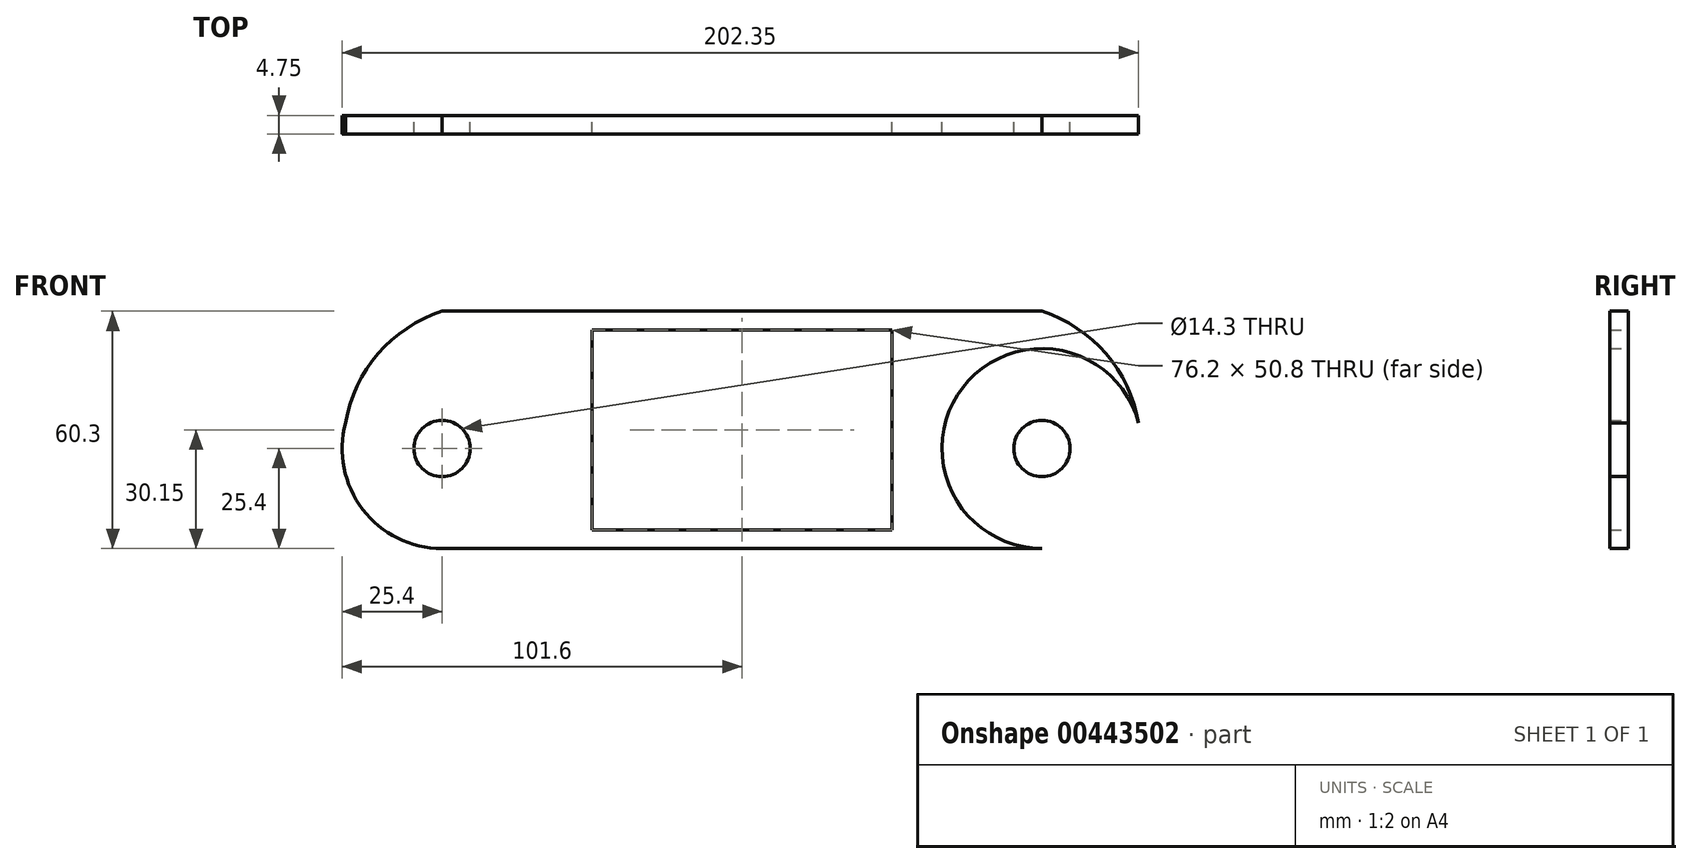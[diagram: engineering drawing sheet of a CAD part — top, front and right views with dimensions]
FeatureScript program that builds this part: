
annotation { "Feature Type Name" : "Feature", "Feature Type Description" : "" }
export const myFeature = defineFeature(function(context is Context, id is Id, definition is map)
    precondition{}
    {
        {
            var Q0;
            Q0=qCreatedBy(makeId("Front.planeOp"),FACE);
            var sketch = newSketch(context, id + "F0", { "sketchPlane" : qUnion([Q0])});
            skLineSegment(sketch, "E0.bottom", {"start": v(-38.1, 30.15) * mm, "end": v(38.1, 30.15) * mm});
            skLineSegment(sketch, "E0.top", {"start": v(-38.1, -20.65) * mm, "end": v(38.1, -20.65) * mm});
            skLineSegment(sketch, "E0.left", {"start": v(-38.1, 30.15) * mm, "end": v(-38.1, -20.65) * mm});
            skLineSegment(sketch, "E0.right", {"start": v(38.1, 30.15) * mm, "end": v(38.1, -20.65) * mm});
            skCircle(sketch, "E1", {"center": v(-76.2, 0) * mm, "radius": 25.4 * mm});
            skCircle(sketch, "E2", {"center": v(-76.2, 0) * mm, "radius": 7.15 * mm});
            skCircle(sketch, "E3.MirrorC", {"center": v(76.2, 0) * mm, "radius": 25.4 * mm});
            skCircle(sketch, "E4.MirrorC", {"center": v(76.2, 0) * mm, "radius": 7.15 * mm});
            skLineSegment(sketch, "E5", {"start": v(-76.31, -25.4) * mm, "end": v(76.2, -25.4) * mm});
            skLineSegment(sketch, "E6", {"start": v(-76.2, 34.9) * mm, "end": v(76.18, 34.9) * mm});
            skLineSegment(sketch, "E7", {"start": v(76.18, 34.9) * mm, "end": v(76.2, 34.9) * mm});
            skArc(sketch, "E8", {"start": v(100.75, 6.5) * mm, "mid": v(92.4, 24.09) * mm, "end": v(76.2, 34.9) * mm});
            skArc(sketch, "E9.MirrorCS", {"start": v(-100.75, 6.5) * mm, "mid": v(-92.4, 24.09) * mm, "end": v(-76.2, 34.9) * mm});
            skSolve(sketch);
        }
        {
            var Q0;
            Q0=makeQuery(id+"F0.imprint","IMPRINT",FACE,{"disambiguationData":[TD([[makeQuery(id+"F0.imprint","IMPRINT",EDGE,{"derivedFrom":sQuery(id+"F0.wireOp",EDGE,"E0.bottom")}),1.0]])]});
            var Q1;
            Q1=makeQuery(id+"F0.imprint","IMPRINT",FACE,{"disambiguationData":[TD([[makeQuery(id+"F0.imprint","IMPRINT",EDGE,{"derivedFrom":sQuery(id+"F0.wireOp",EDGE,"E4.MirrorC")}),1.0]])]});
            var Q2;
            Q2=makeQuery(id+"F0.imprint","IMPRINT",FACE,{"disambiguationData":[TD([[makeQuery(id+"F0.imprint","IMPRINT",EDGE,{"derivedFrom":sQuery(id+"F0.wireOp",EDGE,"E2")}),-1.0]])]});
            extrude(context, id + "F1", {"entities" : qUnion([Q0, Q1, Q2]), "depth" : 4.75 * mm});
        }
    });
